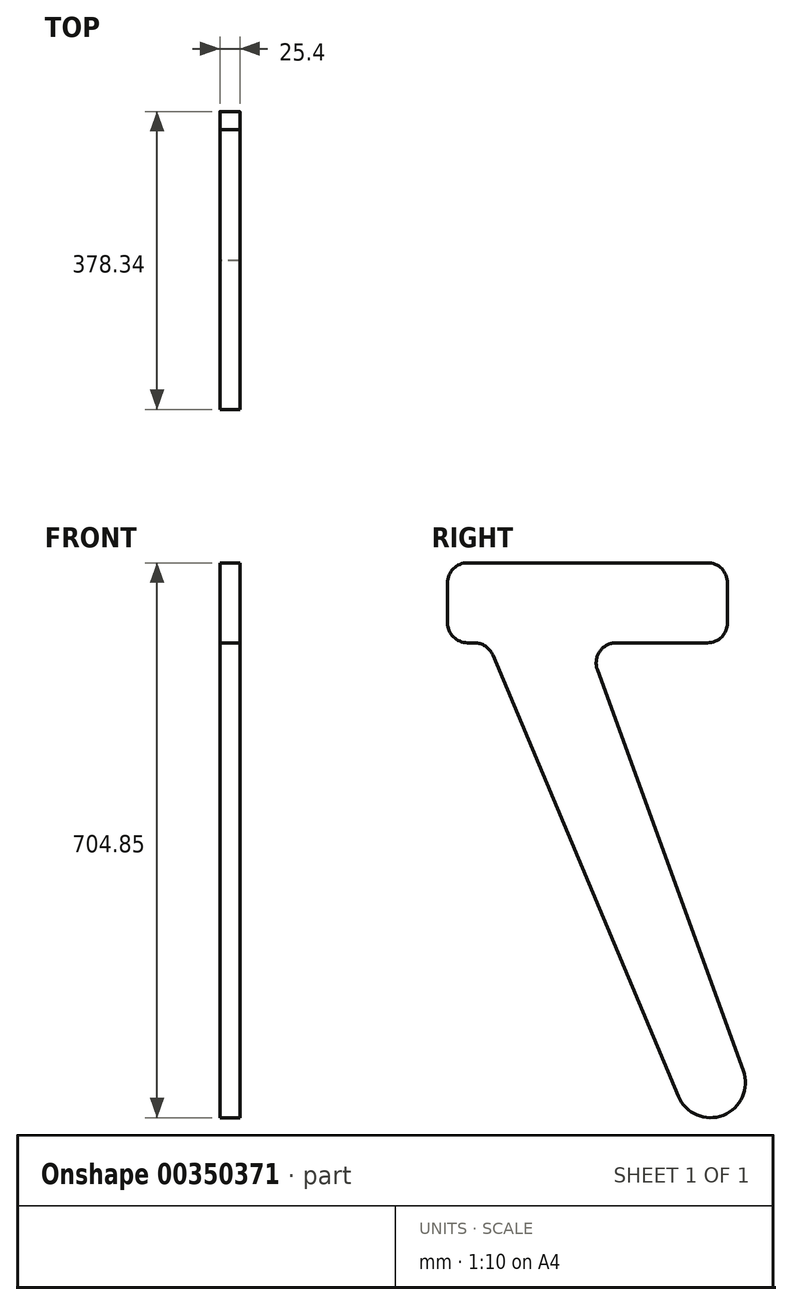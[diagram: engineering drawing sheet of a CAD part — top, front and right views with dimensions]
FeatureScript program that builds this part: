
annotation { "Feature Type Name" : "Feature", "Feature Type Description" : "" }
export const myFeature = defineFeature(function(context is Context, id is Id, definition is map)
    precondition{}
    {
        {
            var Q0;
            Q0=qCreatedBy(makeId("Right.planeOp"),FACE);
            var sketch = newSketch(context, id + "F0", { "sketchPlane" : qUnion([Q0])});
            skLineSegment(sketch, "E0.bottom", {"start": v(246.72, 0) * mm, "end": v(130.6, 0) * mm});
            skLineSegment(sketch, "E0.top", {"start": v(246.72, 101.6) * mm, "end": v(-58.08, 101.6) * mm});
            skLineSegment(sketch, "E0.left", {"start": v(272.12, 25.4) * mm, "end": v(272.12, 76.2) * mm});
            skLineSegment(sketch, "E0.right", {"start": v(-83.48, 25.4) * mm, "end": v(-83.48, 76.2) * mm});
            skPoint(sketch, "E0.middle", {"position": v(94.32, 50.8) * mm});
            skLineSegment(sketch, "E1", {"start": v(-26.14, -15.56) * mm, "end": v(209.43, -576.02) * mm});
            skLineSegment(sketch, "E2", {"start": v(106.73, -34.09) * mm, "end": v(292.18, -543.6) * mm});
            skArc(sketch, "E3", {"start": v(209.43, -576.02) * mm, "mid": v(266.62, -600.19) * mm, "end": v(292.18, -543.6) * mm});
            skLineSegment(sketch, "E4.trimOffspring", {"start": v(-49.55, 0) * mm, "end": v(-58.08, 0) * mm});
            skPoint(sketch, "E5.visualSharp", {"position": v(94.32, 0) * mm});
            skArc(sketch, "E5.filletArc", {"start": v(130.6, 0) * mm, "mid": v(109.8, -10.83) * mm, "end": v(106.73, -34.09) * mm});
            skPoint(sketch, "E6.visualSharp", {"position": v(-32.68, 0) * mm});
            skArc(sketch, "E6.filletArc", {"start": v(-26.14, -15.56) * mm, "mid": v(-35.5, -4.24) * mm, "end": v(-49.55, 0) * mm});
            skPoint(sketch, "E7.visualSharp", {"position": v(-83.48, 0) * mm});
            skArc(sketch, "E7.filletArc", {"start": v(-83.48, 25.4) * mm, "mid": v(-76.04, 7.44) * mm, "end": v(-58.08, 0) * mm});
            skPoint(sketch, "E8.visualSharp", {"position": v(-83.48, 101.6) * mm});
            skArc(sketch, "E8.filletArc", {"start": v(-58.08, 101.6) * mm, "mid": v(-76.04, 94.16) * mm, "end": v(-83.48, 76.2) * mm});
            skPoint(sketch, "E9.visualSharp", {"position": v(272.12, 101.6) * mm});
            skArc(sketch, "E9.filletArc", {"start": v(272.12, 76.2) * mm, "mid": v(264.68, 94.16) * mm, "end": v(246.72, 101.6) * mm});
            skPoint(sketch, "E10.visualSharp", {"position": v(272.12, 0) * mm});
            skArc(sketch, "E10.filletArc", {"start": v(246.72, 0) * mm, "mid": v(264.68, 7.44) * mm, "end": v(272.12, 25.4) * mm});
            skSolve(sketch);
        }
        {
            var Q0;
            Q0=makeQuery(id+"F0.imprint","IMPRINT",FACE,{"disambiguationData":[TD([[makeQuery(id+"F0.imprint","IMPRINT",EDGE,{"derivedFrom":sQuery(id+"F0.wireOp",EDGE,"E0.bottom")}),-1.0]])]});
            extrude(context, id + "F1", {"entities" : qUnion([Q0]), "endBound" : BoundingType.SYMMETRIC, "depth" : 25.4 * mm});
        }
    });
